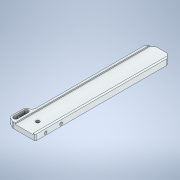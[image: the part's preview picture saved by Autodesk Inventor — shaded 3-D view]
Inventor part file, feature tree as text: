
AUTODESK INVENTOR PART (.ipt)
format: ipt  version: 2020 (Build 240168000, 168)  size: 137,216 bytes
history: native  units: in
note: dims shown in document units (in); Inventor stores cm internally (conversion verified against a paired STEP export)
features: mirror x1
ambient origin geometry x8: Origin, YZ Plane, XZ Plane, XY Plane, X Axis, Y Axis, Z Axis, Center Point
bodies: Solid3 (feature_tree)
feature tree (1):
  mirror  "Mirror1"
